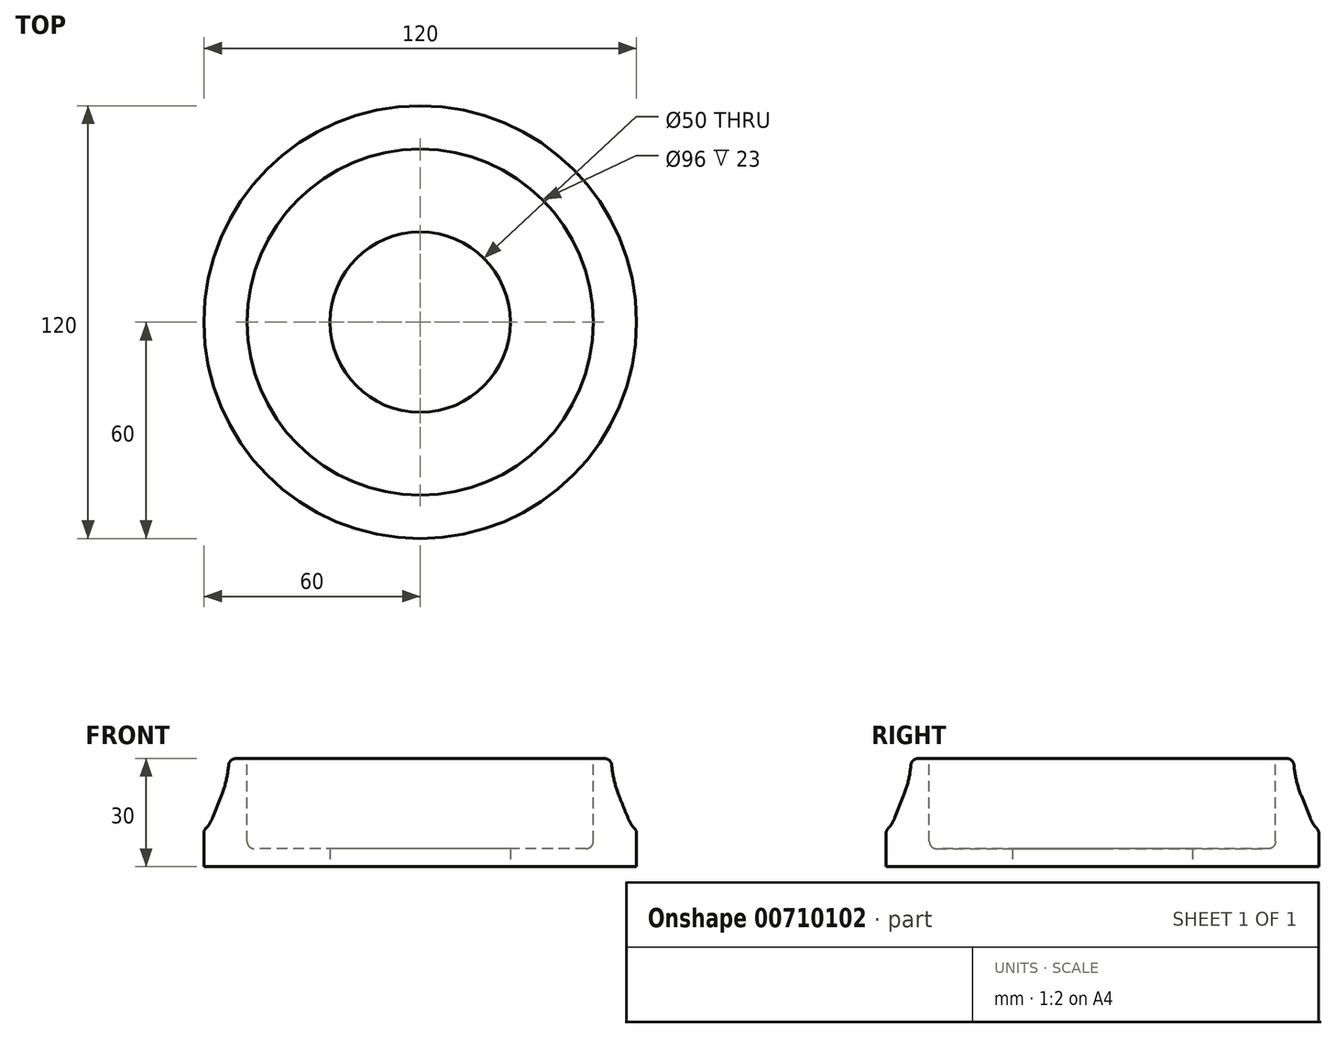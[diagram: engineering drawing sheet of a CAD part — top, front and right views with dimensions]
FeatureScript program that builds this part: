
annotation { "Feature Type Name" : "Feature", "Feature Type Description" : "" }
export const myFeature = defineFeature(function(context is Context, id is Id, definition is map)
    precondition{}
    {
        {
            var Q0;
            Q0=qCreatedBy(makeId("Top.planeOp"),FACE);
            var sketch = newSketch(context, id + "F0", { "sketchPlane" : qUnion([Q0])});
            skCircle(sketch, "E0", {"center": v(0, 0) * mm, "radius": 60 * mm});
            skCircle(sketch, "E1", {"center": v(0, 0) * mm, "radius": 25 * mm});
            skSolve(sketch);
        }
        {
            var Q0;
            Q0=makeQuery(id+"F0.imprint","IMPRINT",FACE,{"disambiguationData":[TD([[makeQuery(id+"F0.imprint","IMPRINT",EDGE,{"derivedFrom":sQuery(id+"F0.wireOp",EDGE,"E0")}),1.0]])]});
            extrude(context, id + "F1", {"entities" : qUnion([Q0]), "depth" : 30 * mm, "offsetDistance" : 25 * mm});
        }
        {
            var Q0;
            Q0=makeQuery(id+"F1.opExtrude","CAP_FACE",FACE,{"disambiguationData":[OSD([sQuery(id+"F0.wireOp",EDGE,"E0"),sQuery(id+"F0.wireOp",EDGE,"E1")])],"isStart":false});
            var sketch = newSketch(context, id + "F2", { "sketchPlane" : qUnion([Q0])});
            skCircle(sketch, "E2", {"center": v(0, 0) * mm, "radius": 48 * mm});
            skSolve(sketch);
        }
        {
            var Q0;
            Q0=makeQuery(id+"F2.imprint","IMPRINT",FACE,{"disambiguationData":[TD([[makeQuery(id+"F2.imprint","IMPRINT",EDGE,{"derivedFrom":sQuery(id+"F2.wireOp",EDGE,"E2")}),1.0]])]});
            extrude(context, id + "F3", {"entities" : qUnion([Q0]), "operationType" : NewBodyOperationType.REMOVE, "oppositeDirection" : true, "depth" : 25 * mm, "offsetDistance" : 25 * mm});
        }
        {
            var Q0;
            Q0=makeQuery(id+"F3.boolean.opBoolean","COPY",EDGE,{"derivedFrom":makeQuery(id+"F3.opExtrude","CAP_EDGE",EDGE,{"disambiguationData":[OSD([sQuery(id+"F2.wireOp",EDGE,"E2")])],"isStart":false})});
            fillet(context, id + "F4", {"entities" : qUnion([Q0]), "radius" : 2 * mm, "tangentPropagation" : true, "allowEdgeOverflow" : false});
        }
        {
            var Q0;
            Q0=makeQuery(id+"F1.opExtrude","CAP_FACE",FACE,{"disambiguationData":[OSD([sQuery(id+"F0.wireOp",EDGE,"E0"),sQuery(id+"F0.wireOp",EDGE,"E1")])],"isStart":false});
            var sketch = newSketch(context, id + "F5", { "sketchPlane" : qUnion([Q0])});
            skCircle(sketch, "E3.0", {"center": v(0, 0) * mm, "radius": 53 * mm});
            skSolve(sketch);
        }
        {
            var Q0;
            Q0=makeQuery(id+"F5.imprint","IMPRINT",FACE,{"disambiguationData":[TD([[makeQuery(id+"F5.imprint","IMPRINT",EDGE,{"derivedFrom":sQuery(id+"F5.wireOp",EDGE,"E3.0")}),-1.0]])]});
            extrude(context, id + "F6", {"entities" : qUnion([Q0]), "operationType" : NewBodyOperationType.REMOVE, "oppositeDirection" : true, "depth" : 20 * mm, "offsetDistance" : 25 * mm});
        }
        {
            var Q0;
            Q0=makeQuery(id+"F6.boolean.opBoolean","COPY",EDGE,{"derivedFrom":makeQuery(id+"F6.opExtrude","CAP_EDGE",EDGE,{"disambiguationData":[OSD([sQuery(id+"F5.wireOp",EDGE,"E3.0")])],"isStart":false})});
            chamfer(context, id + "F7", {"entities" : qUnion([Q0]), "chamferType" : ChamferType.TWO_OFFSETS, "width1" : 15 * mm, "oppositeDirection" : false, "width2" : 6 * mm, "tangentPropagation" : true});
        }
        {
            var Q0;
            {var subQ0=sQuery(id+"F5.wireOp",EDGE,"E3.0");Q0=makeQuery(id+"F7.opChamfer","BLEND_EDGE",EDGE,{"blendedFrom":[makeQuery(id+"F6.boolean.opBoolean","COPY",EDGE,{"derivedFrom":makeQuery(id+"F6.opExtrude","CAP_EDGE",EDGE,{"disambiguationData":[OSD([subQ0])],"isStart":false})}),makeQuery(id+"F6.boolean.opBoolean","COPY",FACE,{"derivedFrom":makeQuery(id+"F6.opExtrude","CAP_FACE",FACE,{"disambiguationData":[OSD([sQuery(id+"F0.wireOp",EDGE,"E0"),subQ0])],"isStart":false})})],"blendedInto":[makeQuery(id+"F6.boolean.opBoolean","COPY",FACE,{"derivedFrom":makeQuery(id+"F6.opExtrude","CAP_FACE",FACE,{"disambiguationData":[OSD([sQuery(id+"F0.wireOp",EDGE,"E0"),subQ0])],"isStart":false})})]});}
            fillet(context, id + "F8", {"entities" : qUnion([Q0]), "radius" : 10 * mm, "tangentPropagation" : true, "allowEdgeOverflow" : false});
        }
        {
            var Q0;
            {var subQ0=sQuery(id+"F5.wireOp",EDGE,"E3.0");Q0=makeQuery(id+"F7.opChamfer","BLEND_EDGE",EDGE,{"blendedFrom":[makeQuery(id+"F6.boolean.opBoolean","COPY",EDGE,{"derivedFrom":makeQuery(id+"F6.opExtrude","CAP_EDGE",EDGE,{"disambiguationData":[OSD([subQ0])],"isStart":false})}),makeQuery(id+"F6.boolean.opBoolean","COPY",FACE,{"derivedFrom":makeQuery(id+"F6.opExtrude","SWEPT_FACE",FACE,{"disambiguationData":[OSD([subQ0])]})})],"blendedInto":[makeQuery(id+"F6.boolean.opBoolean","COPY",FACE,{"derivedFrom":makeQuery(id+"F6.opExtrude","SWEPT_FACE",FACE,{"disambiguationData":[OSD([subQ0])]})})]});}
            fillet(context, id + "F9", {"entities" : qUnion([Q0]), "radius" : 30 * mm, "tangentPropagation" : true, "allowEdgeOverflow" : false});
        }
        {
            var Q0;
            {var subQ0=sQuery(id+"F0.wireOp",EDGE,"E0");var subQ1=sQuery(id+"F5.wireOp",EDGE,"E3.0");Q0=makeQuery(id+"F8.opFillet","BLEND_EDGE",EDGE,{"blendedFrom":[makeQuery(id+"F7.opChamfer","BLEND_EDGE",EDGE,{"blendedFrom":[makeQuery(id+"F6.boolean.opBoolean","COPY",EDGE,{"derivedFrom":makeQuery(id+"F6.opExtrude","CAP_EDGE",EDGE,{"disambiguationData":[OSD([subQ1])],"isStart":false})}),makeQuery(id+"F6.boolean.opBoolean","COPY",FACE,{"derivedFrom":makeQuery(id+"F6.opExtrude","CAP_FACE",FACE,{"disambiguationData":[OSD([subQ0,subQ1])],"isStart":false})})],"blendedInto":[makeQuery(id+"F6.boolean.opBoolean","COPY",FACE,{"derivedFrom":makeQuery(id+"F6.opExtrude","CAP_FACE",FACE,{"disambiguationData":[OSD([subQ0,subQ1])],"isStart":false})})]}),makeQuery(id+"F1.opExtrude","SWEPT_FACE",FACE,{"disambiguationData":[OSD([subQ0])]})],"blendedInto":[makeQuery(id+"F1.opExtrude","SWEPT_FACE",FACE,{"disambiguationData":[OSD([subQ0])]})]});}
            fillet(context, id + "F10", {"entities" : qUnion([Q0]), "radius" : 2 * mm, "tangentPropagation" : true, "allowEdgeOverflow" : false});
        }
        {
            var Q0;
            {var subQ0=sQuery(id+"F5.wireOp",EDGE,"E3.0");Q0=makeQuery(id+"F9.opFillet","BLEND_EDGE",EDGE,{"blendedFrom":[makeQuery(id+"F7.opChamfer","BLEND_EDGE",EDGE,{"blendedFrom":[makeQuery(id+"F6.boolean.opBoolean","COPY",EDGE,{"derivedFrom":makeQuery(id+"F6.opExtrude","CAP_EDGE",EDGE,{"disambiguationData":[OSD([subQ0])],"isStart":false})}),makeQuery(id+"F6.boolean.opBoolean","COPY",FACE,{"derivedFrom":makeQuery(id+"F6.opExtrude","SWEPT_FACE",FACE,{"disambiguationData":[OSD([subQ0])]})})],"blendedInto":[makeQuery(id+"F6.boolean.opBoolean","COPY",FACE,{"derivedFrom":makeQuery(id+"F6.opExtrude","SWEPT_FACE",FACE,{"disambiguationData":[OSD([subQ0])]})})]}),makeQuery(id+"F1.opExtrude","CAP_FACE",FACE,{"disambiguationData":[OSD([sQuery(id+"F0.wireOp",EDGE,"E0"),sQuery(id+"F0.wireOp",EDGE,"E1")])],"isStart":false})],"blendedInto":[makeQuery(id+"F1.opExtrude","CAP_FACE",FACE,{"disambiguationData":[OSD([sQuery(id+"F0.wireOp",EDGE,"E0"),sQuery(id+"F0.wireOp",EDGE,"E1")])],"isStart":false})]});}
            fillet(context, id + "F11", {"entities" : qUnion([Q0]), "radius" : 2 * mm, "tangentPropagation" : true, "allowEdgeOverflow" : false});
        }
    });
